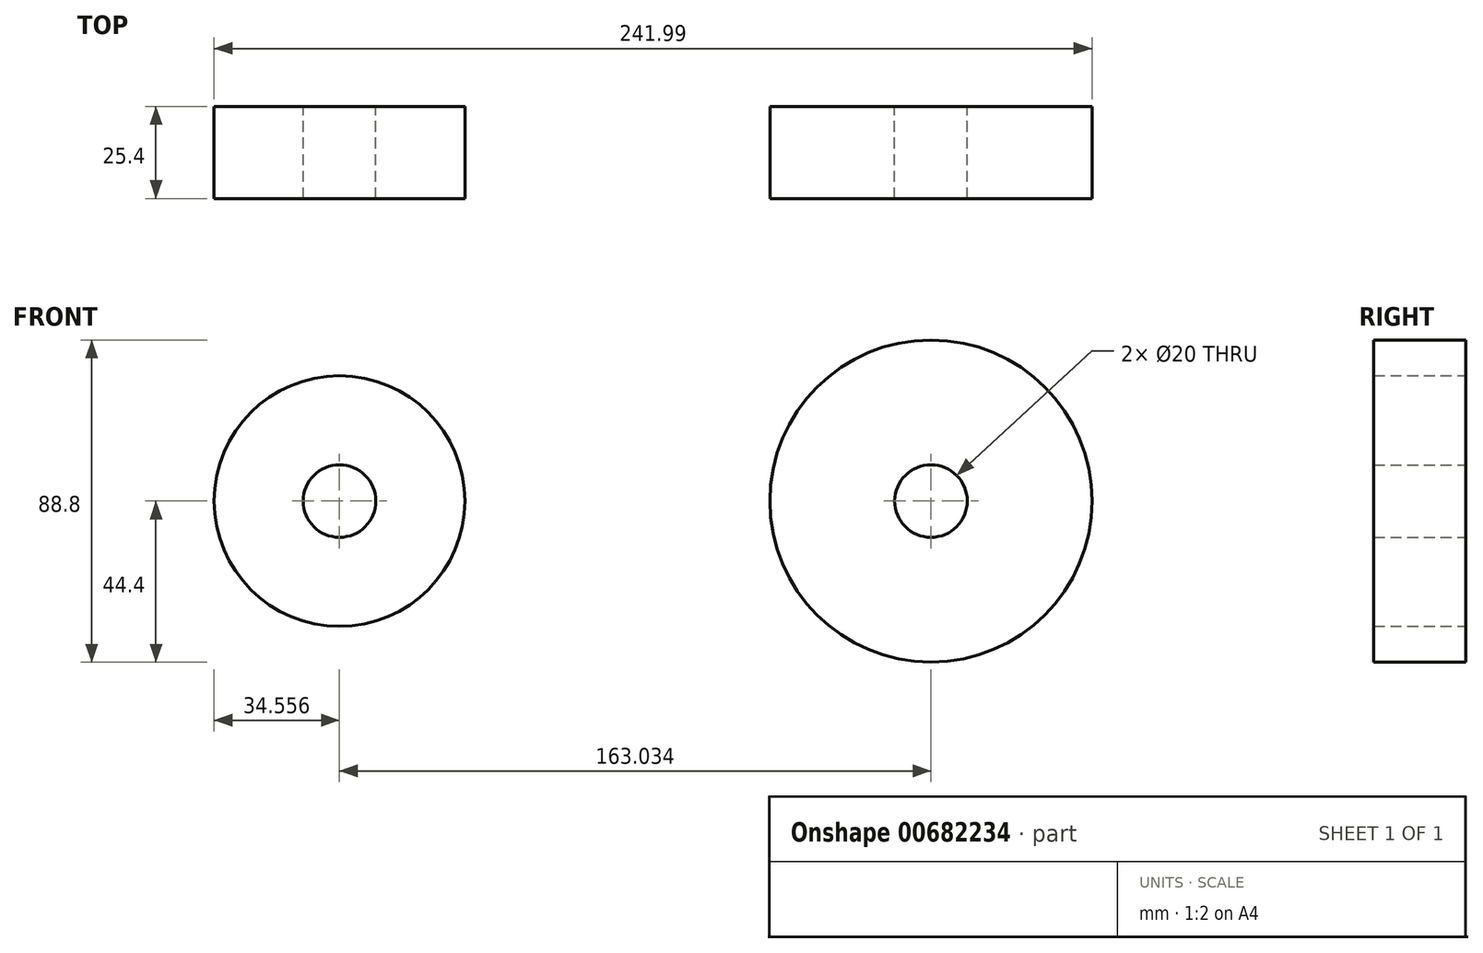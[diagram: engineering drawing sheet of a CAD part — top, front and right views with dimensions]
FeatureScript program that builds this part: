
annotation { "Feature Type Name" : "Feature", "Feature Type Description" : "" }
export const myFeature = defineFeature(function(context is Context, id is Id, definition is map)
    precondition{}
    {
        {
            var Q0;
            Q0=qCreatedBy(makeId("Front.planeOp"),FACE);
            var sketch = newSketch(context, id + "F0", { "sketchPlane" : qUnion([Q0])});
            skCircle(sketch, "E0", {"center": v(0, 0) * mm, "radius": 44.4 * mm});
            skCircle(sketch, "E1", {"center": v(188.67, 0) * mm, "radius": 47.37 * mm});
            skSolve(sketch);
        }
        {
            var Q0;
            Q0=makeQuery(id+"F0.imprint","IMPRINT",FACE,{"disambiguationData":[TD([[makeQuery(id+"F0.imprint","IMPRINT",EDGE,{"derivedFrom":sQuery(id+"F0.wireOp",EDGE,"E0")}),1.0]])]});
            var sketch = newSketch(context, id + "F1", { "sketchPlane" : qUnion([Q0])});
            skSolve(sketch);
        }
        {
            var Q0;
            Q0=makeQuery(id+"F1.imprint","IMPRINT",FACE,{"disambiguationData":[TD([[makeQuery(id+"F1.imprint","IMPRINT",EDGE,{"derivedFrom":makeQuery(id+"F0.imprint","IMPRINT",EDGE,{"derivedFrom":sQuery(id+"F0.wireOp",EDGE,"E0")})}),1.0]])]});
            extrude(context, id + "F2", {"entities" : qUnion([Q0]), "depth" : 25.4 * mm, "offsetDistance" : 25.4 * mm});
        }
        {
            var Q0;
            Q0=sQuery(id+"F0.wireOp",VERTEX,"E0.center");
            var Q1;
            Q1=makeQuery(id+"F2.opExtrude","SWEPT_BODY",BODY,{"disambiguationData":[OSD([sQuery(id+"F0.wireOp",EDGE,"E0")])]});
            hole(context, id + "F3", {"style" : HoleStyle.SIMPLE, "endStyle" : HoleEndStyle.THROUGH, "oppositeDirection" : true, "holeDiameter" : 20 * mm, "majorDiameter" : 6.35 * mm, "isTappedThrough" : true, "tappedDepth" : 12.7 * mm, "tapClearance" : 3, "locations" : qUnion([Q0]), "scope" : qUnion([Q1])});
        }
        {
            var Q0;
            Q0=qCreatedBy(makeId("Front.planeOp"),FACE);
            var sketch = newSketch(context, id + "F4", { "sketchPlane" : qUnion([Q0])});
            skCircle(sketch, "E2", {"center": v(-163.03, 0) * mm, "radius": 34.55 * mm});
            skSolve(sketch);
        }
        {
            var Q0;
            Q0=makeQuery(id+"F4.imprint","IMPRINT",FACE,{"disambiguationData":[TD([[makeQuery(id+"F4.imprint","IMPRINT",EDGE,{"derivedFrom":sQuery(id+"F4.wireOp",EDGE,"E2")}),1.0]])]});
            extrude(context, id + "F5", {"entities" : qUnion([Q0]), "depth" : 25.4 * mm, "offsetDistance" : 25.4 * mm});
        }
        {
            var Q0;
            Q0=sQuery(id+"F4.wireOp",VERTEX,"E2.center");
            var Q1;
            Q1=makeQuery(id+"F5.opExtrude","SWEPT_BODY",BODY,{"disambiguationData":[OSD([sQuery(id+"F4.wireOp",EDGE,"E2")])]});
            hole(context, id + "F6", {"style" : HoleStyle.SIMPLE, "endStyle" : HoleEndStyle.THROUGH, "oppositeDirection" : true, "holeDiameter" : 20 * mm, "majorDiameter" : 6.35 * mm, "isTappedThrough" : true, "tappedDepth" : 12.7 * mm, "tapClearance" : 3, "locations" : qUnion([Q0]), "scope" : qUnion([Q1])});
        }
    });
